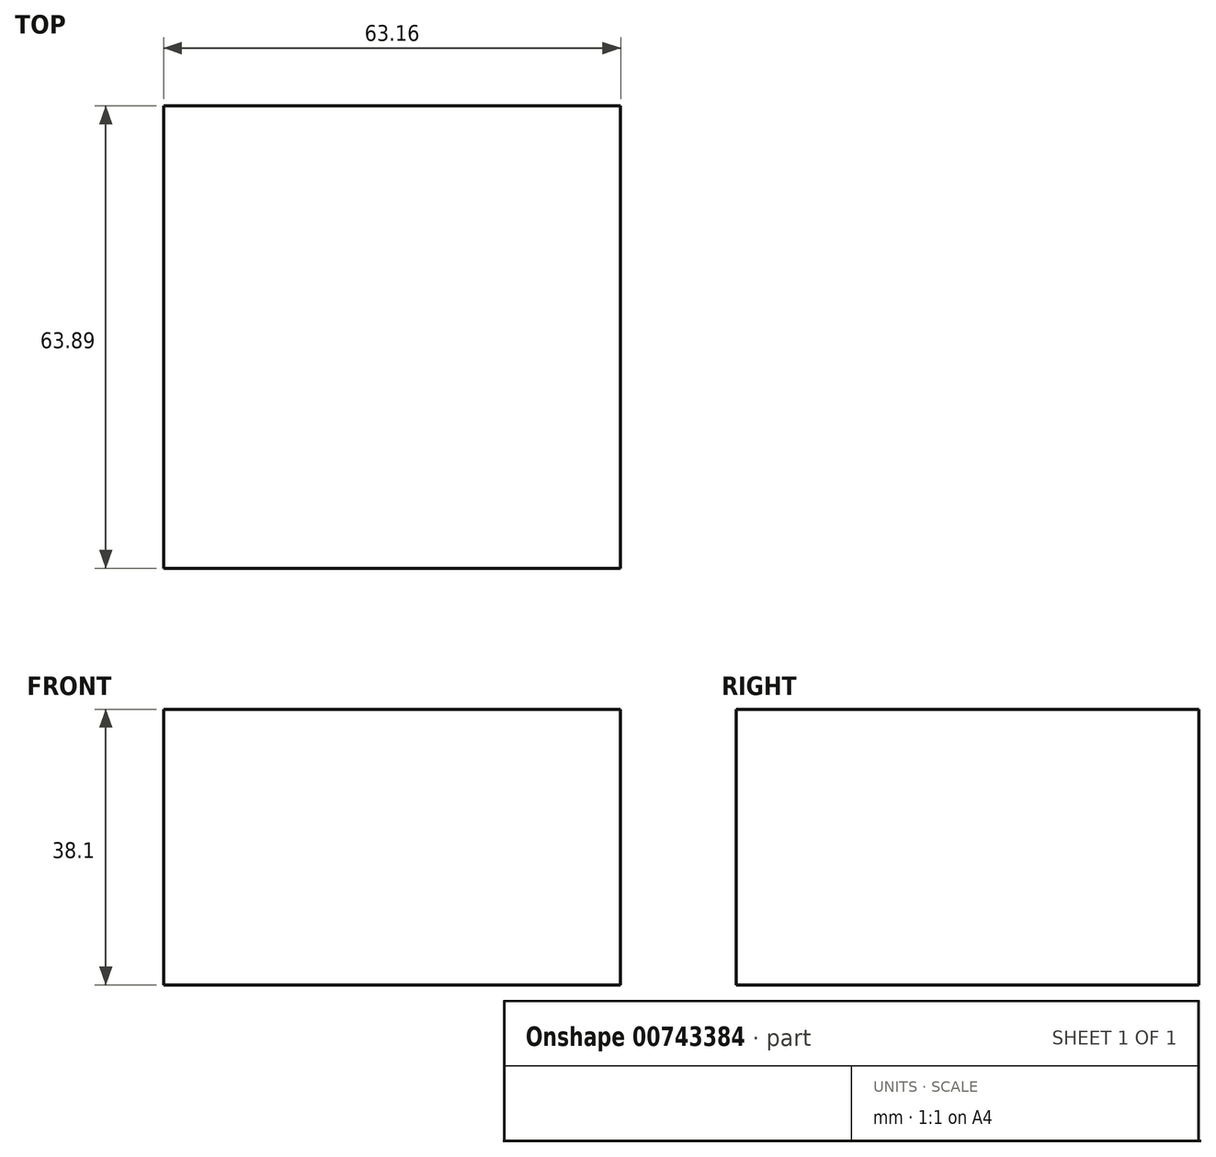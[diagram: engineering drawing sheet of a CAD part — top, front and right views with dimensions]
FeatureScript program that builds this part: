
annotation { "Feature Type Name" : "Feature", "Feature Type Description" : "" }
export const myFeature = defineFeature(function(context is Context, id is Id, definition is map)
    precondition{}
    {
        {
            var Q0;
            Q0=qCreatedBy(makeId("Top.planeOp"),FACE);
            var sketch = newSketch(context, id + "F0", { "sketchPlane" : qUnion([Q0])});
            skLineSegment(sketch, "E0.bottom", {"start": v(-29.72, 0) * mm, "end": v(33.44, 0) * mm});
            skLineSegment(sketch, "E0.top", {"start": v(-29.72, 63.89) * mm, "end": v(33.44, 63.89) * mm});
            skLineSegment(sketch, "E0.left", {"start": v(-29.72, 0) * mm, "end": v(-29.72, 63.89) * mm});
            skLineSegment(sketch, "E0.right", {"start": v(33.44, 0) * mm, "end": v(33.44, 63.89) * mm});
            skSolve(sketch);
        }
        {
            var Q0;
            Q0=makeQuery(id+"F0.imprint","IMPRINT",FACE,{"disambiguationData":[TD([[makeQuery(id+"F0.imprint","IMPRINT",EDGE,{"derivedFrom":sQuery(id+"F0.wireOp",EDGE,"E0.bottom")}),1.0]])]});
            extrude(context, id + "F1", {"entities" : qUnion([Q0]), "depth" : 38.1 * mm, "offsetDistance" : 25.4 * mm});
        }
    });
